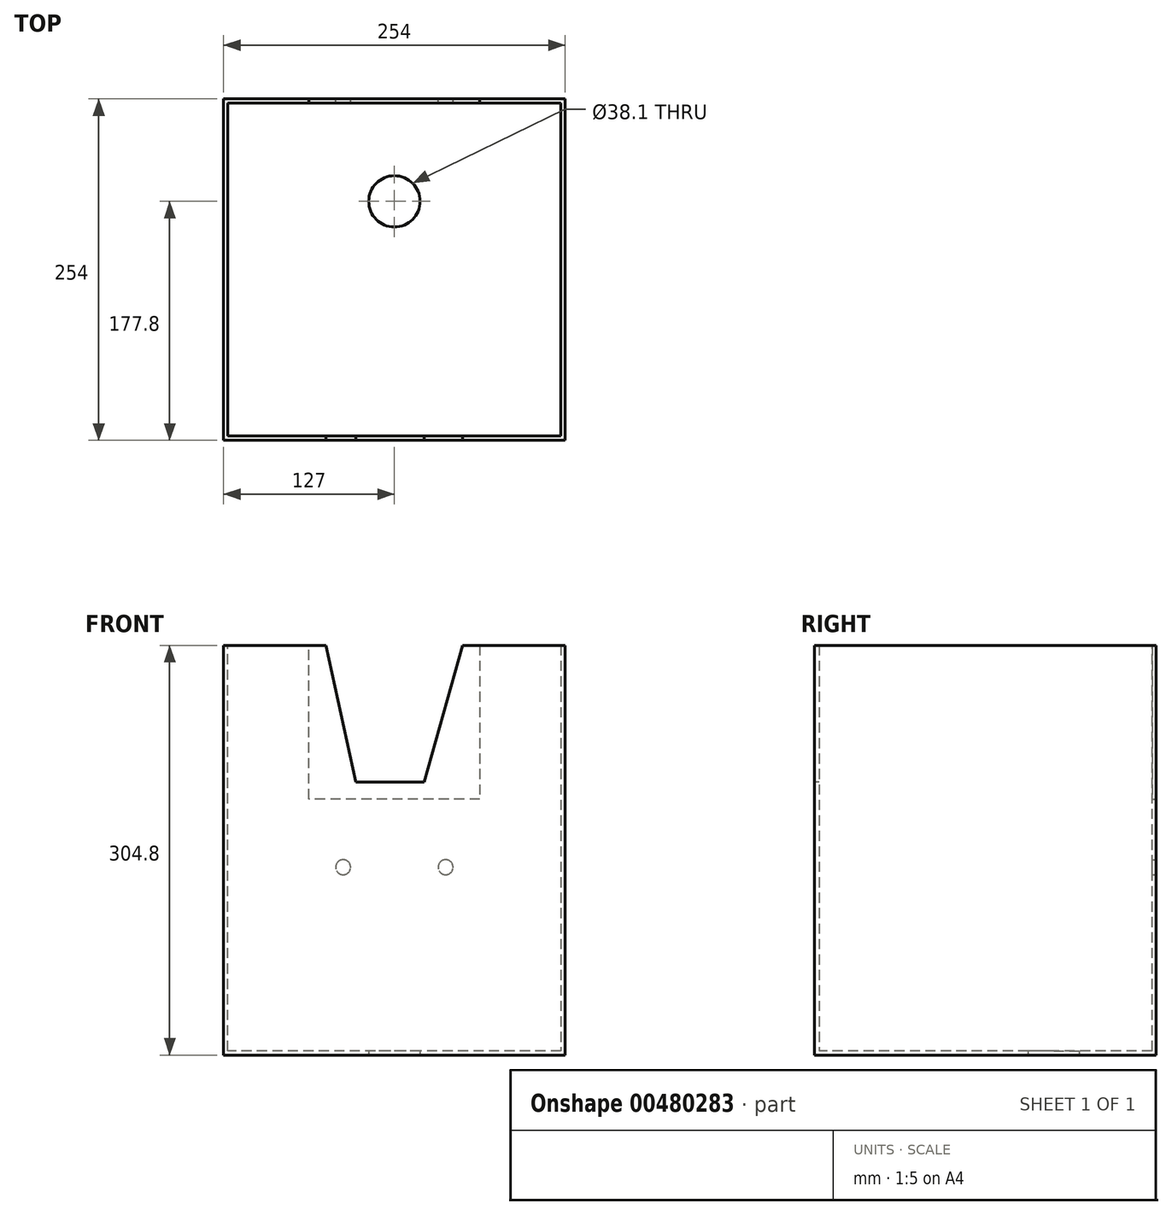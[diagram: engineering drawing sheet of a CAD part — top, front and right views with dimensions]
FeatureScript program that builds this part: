
annotation { "Feature Type Name" : "Feature", "Feature Type Description" : "" }
export const myFeature = defineFeature(function(context is Context, id is Id, definition is map)
    precondition{}
    {
        {
            var Q0;
            Q0=qCreatedBy(makeId("Front.planeOp"),FACE);
            var sketch = newSketch(context, id + "F0", { "sketchPlane" : qUnion([Q0])});
            skLineSegment(sketch, "E0", {"start": v(0, 0) * mm, "end": v(-127, 0) * mm});
            skLineSegment(sketch, "E1", {"start": v(-127, 0) * mm, "end": v(-127, 304.8) * mm});
            skLineSegment(sketch, "E2", {"start": v(-127, 304.8) * mm, "end": v(127, 304.8) * mm});
            skLineSegment(sketch, "E3", {"start": v(127, 304.8) * mm, "end": v(127, 0) * mm});
            skLineSegment(sketch, "E4", {"start": v(127, 0) * mm, "end": v(0, 0) * mm});
            skSolve(sketch);
        }
        {
            var Q0;
            Q0 = qSketchRegion(id + "F0", true);
            extrude(context, id + "F1", {"entities" : qUnion([Q0]), "oppositeDirection" : true, "depth" : 254 * mm});
        }
        {
            var Q0;
            Q0=makeQuery(id+"F1.opExtrude","SWEPT_FACE",FACE,{"disambiguationData":[OSD([sQuery(id+"F0.wireOp",EDGE,"E2")])]});
            shell(context, id + "F2", {"entities" : qUnion([Q0]), "thickness" : 3.17 * mm});
        }
        {
            var Q0;
            Q0=makeQuery(id+"F1.opExtrude","CAP_FACE",FACE,{"disambiguationData":[OSD([sQuery(id+"F0.wireOp",EDGE,"E0"),sQuery(id+"F0.wireOp",EDGE,"E1"),sQuery(id+"F0.wireOp",EDGE,"E2"),sQuery(id+"F0.wireOp",EDGE,"E3"),sQuery(id+"F0.wireOp",EDGE,"E4")])],"isStart":true});
            var sketch = newSketch(context, id + "F3", { "sketchPlane" : qUnion([Q0])});
            skLineSegment(sketch, "E5", {"start": v(-127, 304.8) * mm, "end": v(-50.8, 304.8) * mm});
            skLineSegment(sketch, "E6", {"start": v(-50.8, 304.8) * mm, "end": v(-28.57, 203.2) * mm});
            skLineSegment(sketch, "E7", {"start": v(-28.57, 203.2) * mm, "end": v(-127, 203.2) * mm});
            skLineSegment(sketch, "E8", {"start": v(-28.57, 203.2) * mm, "end": v(22.23, 203.2) * mm});
            skLineSegment(sketch, "E9", {"start": v(22.23, 203.2) * mm, "end": v(50.8, 304.8) * mm});
            skLineSegment(sketch, "E10", {"start": v(50.8, 304.8) * mm, "end": v(-50.8, 304.8) * mm});
            skSolve(sketch);
        }
        {
            var Q0;
            Q0 = qSketchRegion(id + "F3", true);
            extrude(context, id + "F4", {"entities" : qUnion([Q0]), "operationType" : NewBodyOperationType.REMOVE, "oppositeDirection" : true, "depth" : 25.4 * mm});
        }
        {
            var Q0;
            Q0=makeQuery(id+"F1.opExtrude","CAP_FACE",FACE,{"disambiguationData":[OSD([sQuery(id+"F0.wireOp",EDGE,"E0"),sQuery(id+"F0.wireOp",EDGE,"E1"),sQuery(id+"F0.wireOp",EDGE,"E2"),sQuery(id+"F0.wireOp",EDGE,"E3"),sQuery(id+"F0.wireOp",EDGE,"E4")])],"isStart":false});
            var sketch = newSketch(context, id + "F5", { "sketchPlane" : qUnion([Q0])});
            skLineSegment(sketch, "E11", {"start": v(-127, 304.8) * mm, "end": v(-16.94, 304.8) * mm});
            skLineSegment(sketch, "E12", {"start": v(-16.94, 190.5) * mm, "end": v(-63.5, 190.5) * mm});
            skLineSegment(sketch, "E13", {"start": v(-63.5, 190.5) * mm, "end": v(-63.5, 304.8) * mm});
            skLineSegment(sketch, "E14", {"start": v(-63.5, 304.8) * mm, "end": v(63.5, 304.8) * mm});
            skLineSegment(sketch, "E15", {"start": v(63.5, 304.8) * mm, "end": v(63.5, 190.5) * mm});
            skLineSegment(sketch, "E16", {"start": v(63.5, 190.5) * mm, "end": v(-16.94, 190.5) * mm});
            skSolve(sketch);
        }
        {
            var Q0;
            Q0 = qSketchRegion(id + "F5", true);
            extrude(context, id + "F6", {"entities" : qUnion([Q0]), "operationType" : NewBodyOperationType.REMOVE, "oppositeDirection" : true, "depth" : 25.4 * mm});
        }
        {
            var Q0;
            Q0=makeQuery(id+"F1.opExtrude","SWEPT_FACE",FACE,{"disambiguationData":[OSD([sQuery(id+"F0.wireOp",EDGE,"E0"),sQuery(id+"F0.wireOp",EDGE,"E4")])]});
            var sketch = newSketch(context, id + "F7", { "sketchPlane" : qUnion([Q0])});
            skLineSegment(sketch, "E17", {"start": v(0, 0) * mm, "end": v(0, -177.8) * mm});
            skCircle(sketch, "E18", {"center": v(0, -177.8) * mm, "radius": 19.05 * mm});
            skSolve(sketch);
        }
        {
            var Q0;
            Q0 = qSketchRegion(id + "F7", true);
            extrude(context, id + "F8", {"entities" : qUnion([Q0]), "operationType" : NewBodyOperationType.REMOVE, "oppositeDirection" : true, "depth" : 25.4 * mm});
        }
        {
            var Q0;
            Q0=makeQuery(id+"F1.opExtrude","CAP_FACE",FACE,{"disambiguationData":[OSD([sQuery(id+"F0.wireOp",EDGE,"E0"),sQuery(id+"F0.wireOp",EDGE,"E1"),sQuery(id+"F0.wireOp",EDGE,"E2"),sQuery(id+"F0.wireOp",EDGE,"E3"),sQuery(id+"F0.wireOp",EDGE,"E4")])],"isStart":false});
            var sketch = newSketch(context, id + "F9", { "sketchPlane" : qUnion([Q0])});
            skLineSegment(sketch, "E19", {"start": v(0, 190.5) * mm, "end": v(0, 139.7) * mm});
            skLineSegment(sketch, "E20", {"start": v(0, 139.7) * mm, "end": v(38.1, 139.7) * mm});
            skLineSegment(sketch, "E21", {"start": v(38.1, 139.7) * mm, "end": v(-38.1, 139.7) * mm});
            skCircle(sketch, "E22", {"center": v(38.1, 139.7) * mm, "radius": 5.56 * mm});
            skCircle(sketch, "E23", {"center": v(-38.1, 139.7) * mm, "radius": 5.56 * mm});
            skSolve(sketch);
        }
        {
            var Q0;
            Q0 = qSketchRegion(id + "F9", true);
            extrude(context, id + "F10", {"entities" : qUnion([Q0]), "operationType" : NewBodyOperationType.REMOVE, "oppositeDirection" : true, "depth" : 25.4 * mm});
        }
    });
